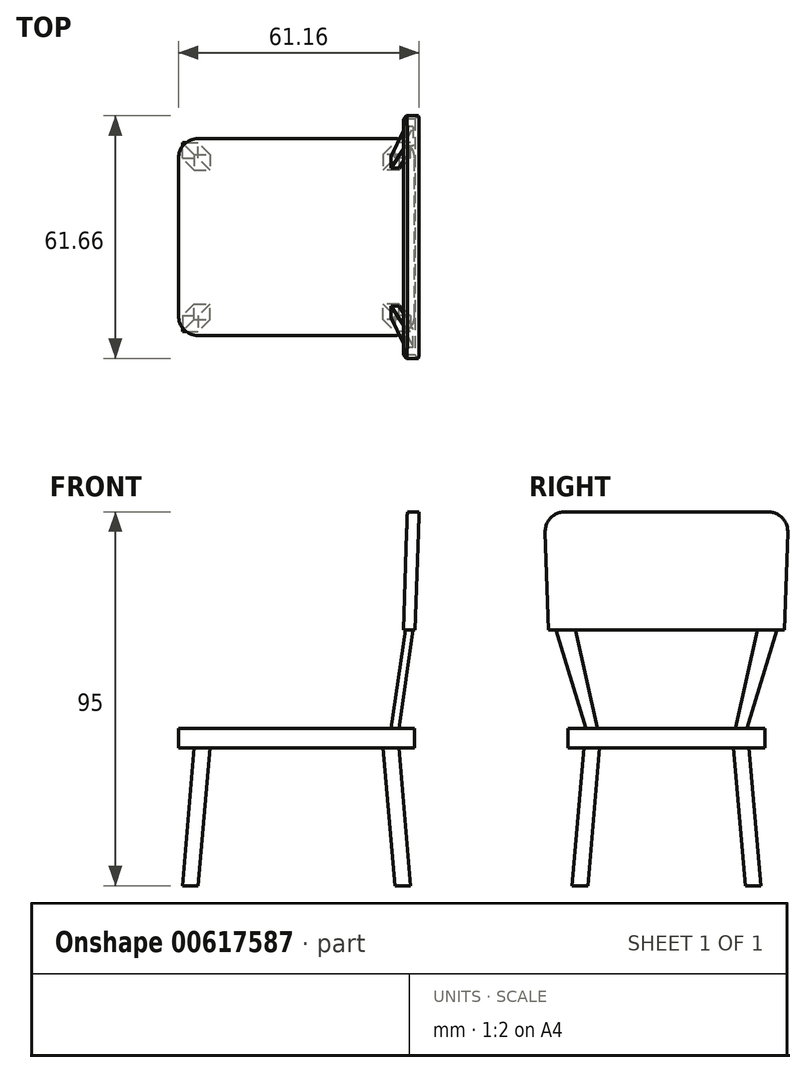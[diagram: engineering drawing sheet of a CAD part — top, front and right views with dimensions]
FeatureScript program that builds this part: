
annotation { "Feature Type Name" : "Feature", "Feature Type Description" : "" }
export const myFeature = defineFeature(function(context is Context, id is Id, definition is map)
    precondition{}
    {
        {
            var Q0;
            Q0=qCreatedBy(makeId("Top.planeOp"),FACE);
            var sketch = newSketch(context, id + "F0", { "sketchPlane" : qUnion([Q0])});
            skLineSegment(sketch, "E0.bottom", {"start": v(0, 0) * mm, "end": v(-30, 0) * mm});
            skLineSegment(sketch, "E0.top", {"start": v(0, 25) * mm, "end": v(-25, 25) * mm});
            skLineSegment(sketch, "E0.left", {"start": v(0, 0) * mm, "end": v(0, 25) * mm});
            skLineSegment(sketch, "E0.right", {"start": v(-30, 0) * mm, "end": v(-30, 20) * mm});
            skPoint(sketch, "E1.visualSharp", {"position": v(-30, 25) * mm});
            skArc(sketch, "E1.filletArc", {"start": v(-25, 25) * mm, "mid": v(-28.54, 23.54) * mm, "end": v(-30, 20) * mm});
            skSolve(sketch);
        }
        {
            var Q0;
            Q0 = qSketchRegion(id + "F0", true);
            extrude(context, id + "F1", {"entities" : qUnion([Q0]), "depth" : 5 * mm, "offsetDistance" : 25 * mm});
        }
        {
            var Q0;
            Q0=makeQuery(id+"F1.opExtrude","CAP_FACE",FACE,{"disambiguationData":[OSD([sQuery(id+"F0.wireOp",EDGE,"E0.bottom"),sQuery(id+"F0.wireOp",EDGE,"E0.top"),sQuery(id+"F0.wireOp",EDGE,"E0.left"),sQuery(id+"F0.wireOp",EDGE,"E0.right"),sQuery(id+"F0.wireOp",EDGE,"E1.filletArc")])],"isStart":true});
            var sketch = newSketch(context, id + "F2", { "sketchPlane" : qUnion([Q0])});
            skLineSegment(sketch, "E2.bottom", {"start": v(-26, -21) * mm, "end": v(-22, -21) * mm});
            skLineSegment(sketch, "E2.top", {"start": v(-26, -17) * mm, "end": v(-22, -17) * mm});
            skLineSegment(sketch, "E2.left", {"start": v(-26, -21) * mm, "end": v(-26, -17) * mm});
            skLineSegment(sketch, "E2.right", {"start": v(-22, -21) * mm, "end": v(-22, -17) * mm});
            skSolve(sketch);
        }
        {
            var Q0;
            Q0=makeQuery(id+"F2.imprint","IMPRINT",FACE,{"disambiguationData":[TD([[makeQuery(id+"F2.imprint","IMPRINT",EDGE,{"derivedFrom":sQuery(id+"F2.wireOp",EDGE,"E2.bottom")}),-1.0]])]});
            cPlane(context, id + "F3", {"entities" : qUnion([Q0]), "cplaneType" : CPlaneType.OFFSET, "offset" : 35 * mm, "width" : 150 * mm, "height" : 150 * mm});
        }
        {
            var Q0;
            Q0=qCreatedBy(id+"F3.planeOp",FACE);
            var sketch = newSketch(context, id + "F4", { "sketchPlane" : qUnion([Q0])});
            skLineSegment(sketch, "E3.bottom", {"start": v(-29, -20) * mm, "end": v(-25, -20) * mm});
            skLineSegment(sketch, "E3.top", {"start": v(-29, -24) * mm, "end": v(-25, -24) * mm});
            skLineSegment(sketch, "E3.left", {"start": v(-29, -20) * mm, "end": v(-29, -24) * mm});
            skLineSegment(sketch, "E3.right", {"start": v(-25, -20) * mm, "end": v(-25, -24) * mm});
            skSolve(sketch);
        }
        {
            var Q1;
            Q1=makeQuery(id+"F2.imprint","IMPRINT",FACE,{"disambiguationData":[TD([[makeQuery(id+"F2.imprint","IMPRINT",EDGE,{"derivedFrom":sQuery(id+"F2.wireOp",EDGE,"E2.bottom")}),1.0]])]});
            var Q2;
            Q2=makeQuery(id+"F4.imprint","IMPRINT",FACE,{"disambiguationData":[TD([[makeQuery(id+"F4.imprint","IMPRINT",EDGE,{"derivedFrom":sQuery(id+"F4.wireOp",EDGE,"E3.bottom")}),-1.0]])]});
            loft(context, id + "F5", {"operationType" : NewBodyOperationType.ADD, "sheetProfilesArray" : [{ "sheetProfileEntities" : qUnion([Q1]) }, { "sheetProfileEntities" : qUnion([Q2]) }]});
        }
        {
            var Q0;
            Q0=makeQuery(id+"F1.opExtrude","SWEPT_BODY",BODY,{"disambiguationData":[OSD([sQuery(id+"F0.wireOp",EDGE,"E0.bottom"),sQuery(id+"F0.wireOp",EDGE,"E0.top"),sQuery(id+"F0.wireOp",EDGE,"E0.left"),sQuery(id+"F0.wireOp",EDGE,"E0.right"),sQuery(id+"F0.wireOp",EDGE,"E1.filletArc")])]});
            var Q1;
            Q1=qCreatedBy(makeId("Right.planeOp"),FACE);
            mirror(context, id + "F6", {"operationType" : NewBodyOperationType.ADD, "entities" : qUnion([Q0]), "mirrorPlane" : qUnion([Q1])});
        }
        {
            var Q0;
            {var subQ0=makeQuery(id+"F1.opExtrude","CAP_FACE",FACE,{"disambiguationData":[OSD([sQuery(id+"F0.wireOp",EDGE,"E0.bottom"),sQuery(id+"F0.wireOp",EDGE,"E0.top"),sQuery(id+"F0.wireOp",EDGE,"E0.left"),sQuery(id+"F0.wireOp",EDGE,"E0.right"),sQuery(id+"F0.wireOp",EDGE,"E1.filletArc")])],"isStart":false});Q0=makeQuery(id+"F6.boolean.opBoolean","MERGE",FACE,{"derivedFrom":[subQ0,makeQuery(id+"F6.opPattern","COPY",FACE,{"derivedFrom":subQ0,"instanceName":"1"})]});}
            var sketch = newSketch(context, id + "F7", { "sketchPlane" : qUnion([Q0])});
            skLineSegment(sketch, "E4.bottom", {"start": v(25.98, 20.5) * mm, "end": v(23.98, 20.5) * mm});
            skLineSegment(sketch, "E4.top", {"start": v(25.98, 17.5) * mm, "end": v(23.98, 17.5) * mm});
            skLineSegment(sketch, "E4.left", {"start": v(25.98, 20.5) * mm, "end": v(25.98, 17.5) * mm});
            skLineSegment(sketch, "E4.right", {"start": v(23.98, 20.5) * mm, "end": v(23.98, 17.5) * mm});
            skSolve(sketch);
        }
        {
            var Q0;
            Q0=makeQuery(id+"F7.imprint","IMPRINT",FACE,{"disambiguationData":[TD([[makeQuery(id+"F7.imprint","IMPRINT",EDGE,{"derivedFrom":sQuery(id+"F7.wireOp",EDGE,"E4.bottom")}),-1.0]])]});
            cPlane(context, id + "F8", {"entities" : qUnion([Q0]), "cplaneType" : CPlaneType.OFFSET, "offset" : 25 * mm, "width" : 150 * mm, "height" : 150 * mm});
        }
        {
            var Q0;
            Q0=qCreatedBy(id+"F8.planeOp",FACE);
            var sketch = newSketch(context, id + "F9", { "sketchPlane" : qUnion([Q0])});
            skLineSegment(sketch, "E5.bottom", {"start": v(29.66, 28.11) * mm, "end": v(27.66, 28.11) * mm});
            skLineSegment(sketch, "E5.top", {"start": v(29.66, 23.11) * mm, "end": v(27.66, 23.11) * mm});
            skLineSegment(sketch, "E5.left", {"start": v(29.66, 28.11) * mm, "end": v(29.66, 23.11) * mm});
            skLineSegment(sketch, "E5.right", {"start": v(27.66, 28.11) * mm, "end": v(27.66, 23.11) * mm});
            skSolve(sketch);
        }
        {
            var Q1;
            Q1=makeQuery(id+"F7.imprint","IMPRINT",FACE,{"disambiguationData":[TD([[makeQuery(id+"F7.imprint","IMPRINT",EDGE,{"derivedFrom":sQuery(id+"F7.wireOp",EDGE,"E4.bottom")}),1.0]])]});
            var Q2;
            Q2=makeQuery(id+"F9.imprint","IMPRINT",FACE,{"disambiguationData":[TD([[makeQuery(id+"F9.imprint","IMPRINT",EDGE,{"derivedFrom":sQuery(id+"F9.wireOp",EDGE,"E5.bottom")}),1.0]])]});
            loft(context, id + "F10", {"operationType" : NewBodyOperationType.ADD, "sheetProfilesArray" : [{ "sheetProfileEntities" : qUnion([Q1]) }, { "sheetProfileEntities" : qUnion([Q2]) }]});
        }
        {
            var Q0;
            Q0=qCreatedBy(id+"F8.planeOp",FACE);
            var sketch = newSketch(context, id + "F11", { "sketchPlane" : qUnion([Q0])});
            skLineSegment(sketch, "E6.bottom", {"start": v(30.16, 30) * mm, "end": v(27.16, 30) * mm});
            skLineSegment(sketch, "E6.top", {"start": v(30.16, 0) * mm, "end": v(27.16, 0) * mm});
            skLineSegment(sketch, "E6.left", {"start": v(30.16, 30) * mm, "end": v(30.16, 0) * mm});
            skLineSegment(sketch, "E6.right", {"start": v(27.16, 30) * mm, "end": v(27.16, 0) * mm});
            skSolve(sketch);
        }
        {
            var Q0;
            Q0=qCreatedBy(id+"F8.planeOp",FACE);
            cPlane(context, id + "F12", {"entities" : qUnion([Q0]), "cplaneType" : CPlaneType.OFFSET, "offset" : 30 * mm, "width" : 150 * mm, "height" : 150 * mm});
        }
        {
            var Q0;
            Q0=qCreatedBy(id+"F12.planeOp",FACE);
            var sketch = newSketch(context, id + "F13", { "sketchPlane" : qUnion([Q0])});
            skLineSegment(sketch, "E7.bottom", {"start": v(28.16, 31) * mm, "end": v(31.16, 31) * mm});
            skLineSegment(sketch, "E7.top", {"start": v(28.16, 0) * mm, "end": v(31.16, 0) * mm});
            skLineSegment(sketch, "E7.left", {"start": v(28.16, 31) * mm, "end": v(28.16, 0) * mm});
            skLineSegment(sketch, "E7.right", {"start": v(31.16, 31) * mm, "end": v(31.16, 0) * mm});
            skSolve(sketch);
        }
        {
            var Q1;
            Q1=makeQuery(id+"F11.imprint","IMPRINT",FACE,{"disambiguationData":[TD([[makeQuery(id+"F11.imprint","IMPRINT",EDGE,{"derivedFrom":sQuery(id+"F11.wireOp",EDGE,"E6.bottom")}),1.0]])]});
            var Q2;
            Q2=makeQuery(id+"F13.imprint","IMPRINT",FACE,{"disambiguationData":[TD([[makeQuery(id+"F13.imprint","IMPRINT",EDGE,{"derivedFrom":sQuery(id+"F13.wireOp",EDGE,"E7.bottom")}),-1.0]])]});
            loft(context, id + "F14", {"operationType" : NewBodyOperationType.ADD, "sheetProfilesArray" : [{ "sheetProfileEntities" : qUnion([Q1]) }, { "sheetProfileEntities" : qUnion([Q2]) }]});
        }
        {
            var Q0;
            Q0=makeQuery(id+"F1.opExtrude","SWEPT_BODY",BODY,{"disambiguationData":[OSD([sQuery(id+"F0.wireOp",EDGE,"E0.bottom"),sQuery(id+"F0.wireOp",EDGE,"E0.top"),sQuery(id+"F0.wireOp",EDGE,"E0.left"),sQuery(id+"F0.wireOp",EDGE,"E0.right"),sQuery(id+"F0.wireOp",EDGE,"E1.filletArc")])]});
            var Q1;
            Q1=qCreatedBy(makeId("Front.planeOp"),FACE);
            mirror(context, id + "F15", {"operationType" : NewBodyOperationType.ADD, "entities" : qUnion([Q0]), "mirrorPlane" : qUnion([Q1])});
        }
        {
            var Q0;
            Q0=makeQuery(id+"F15.opPattern","COPY",EDGE,{"derivedFrom":makeQuery(id+"F14.opLoft","MID_CAP_EDGE",EDGE,{"disambiguationData":[OSD([sQuery(id+"F13.wireOp",EDGE,"E7.bottom"),sQuery(id+"F13.wireOp",EDGE,"E7.left"),sQuery(id+"F13.wireOp",EDGE,"E7.right")])],"capPos":1.0}),"instanceName":"1"});
            var Q1;
            Q1=makeQuery(id+"F14.opLoft","MID_CAP_EDGE",EDGE,{"disambiguationData":[OSD([sQuery(id+"F13.wireOp",EDGE,"E7.bottom"),sQuery(id+"F13.wireOp",EDGE,"E7.left"),sQuery(id+"F13.wireOp",EDGE,"E7.right")])],"capPos":1.0});
            fillet(context, id + "F16", {"entities" : qUnion([Q0, Q1]), "radius" : 5 * mm, "tangentPropagation" : true, "allowEdgeOverflow" : false});
        }
        {
            var Q0;
            Q0=makeQuery(id+"F1.opExtrude","SWEPT_BODY",BODY,{"disambiguationData":[OSD([sQuery(id+"F0.wireOp",EDGE,"E0.bottom"),sQuery(id+"F0.wireOp",EDGE,"E0.top"),sQuery(id+"F0.wireOp",EDGE,"E0.left"),sQuery(id+"F0.wireOp",EDGE,"E0.right"),sQuery(id+"F0.wireOp",EDGE,"E1.filletArc")])]});
            var Q1;
            Q1=qCreatedBy(makeId("Front.planeOp"),FACE);
            mirror(context, id + "F17", {"operationType" : NewBodyOperationType.ADD, "entities" : qUnion([Q0]), "mirrorPlane" : qUnion([Q1])});
        }
    });
